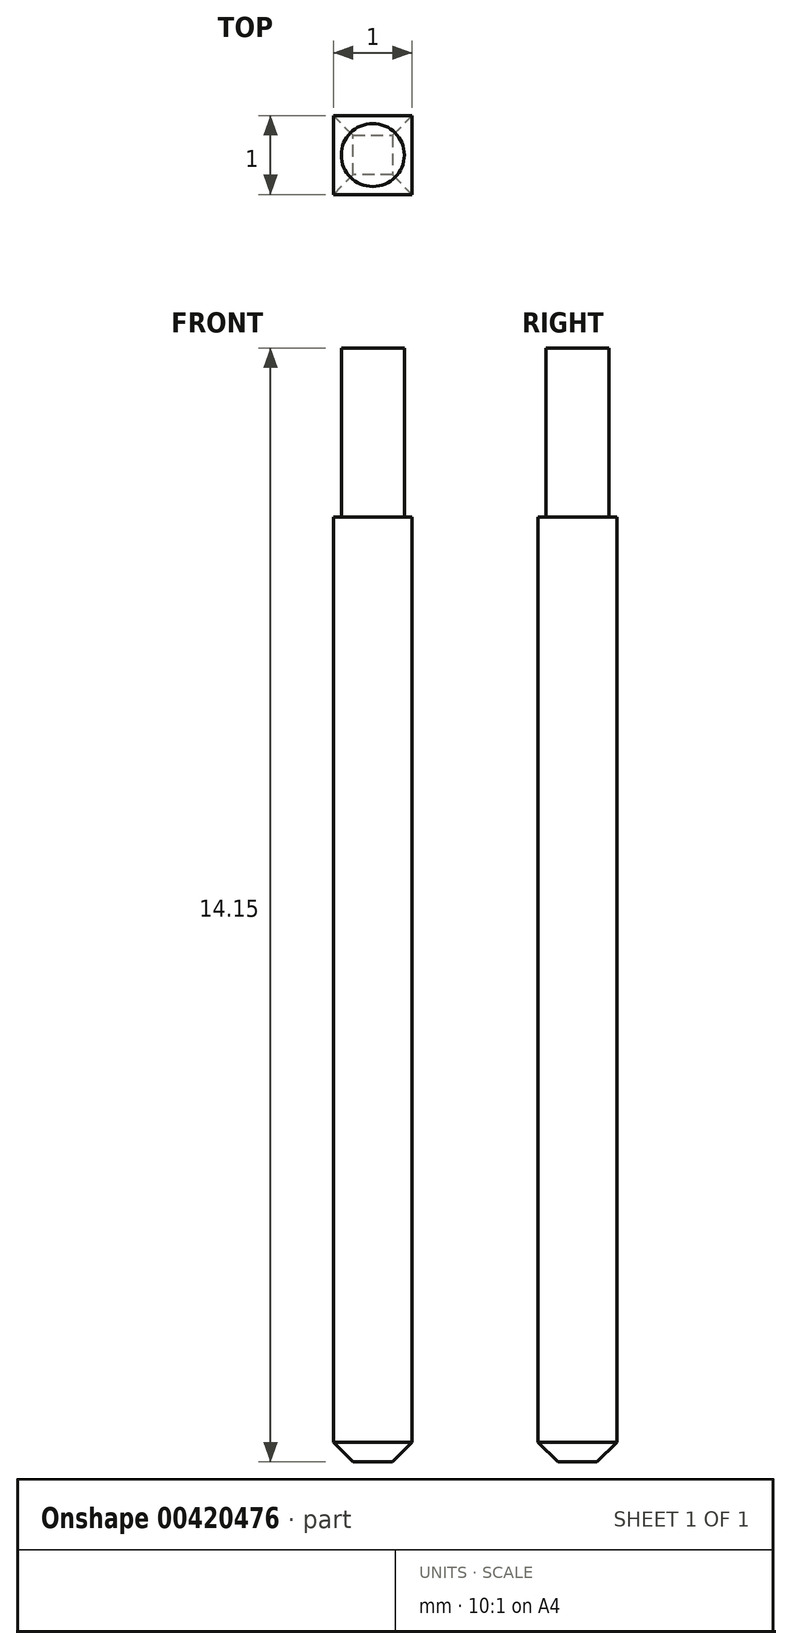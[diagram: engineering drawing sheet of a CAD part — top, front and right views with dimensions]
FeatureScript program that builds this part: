
annotation { "Feature Type Name" : "Feature", "Feature Type Description" : "" }
export const myFeature = defineFeature(function(context is Context, id is Id, definition is map)
    precondition{}
    {
        {
            var Q0;
            Q0=qCreatedBy(makeId("Top.planeOp"),FACE);
            var sketch = newSketch(context, id + "F0", { "sketchPlane" : qUnion([Q0])});
            skLineSegment(sketch, "E0.bottom", {"start": v(0, 0) * mm, "end": v(1, 0) * mm});
            skLineSegment(sketch, "E0.top", {"start": v(0, 1) * mm, "end": v(1, 1) * mm});
            skLineSegment(sketch, "E0.left", {"start": v(0, 0) * mm, "end": v(0, 1) * mm});
            skLineSegment(sketch, "E0.right", {"start": v(1, 0) * mm, "end": v(1, 1) * mm});
            skSolve(sketch);
        }
        {
            var Q0;
            Q0 = qSketchRegion(id + "F0", true);
            extrude(context, id + "F1", {"entities" : qUnion([Q0]), "depth" : 12 * mm});
        }
        {
            var Q0;
            Q0=makeQuery(id+"F1.opExtrude","CAP_FACE",FACE,{"disambiguationData":[OSD([sQuery(id+"F0.wireOp",EDGE,"E0.bottom"),sQuery(id+"F0.wireOp",EDGE,"E0.top"),sQuery(id+"F0.wireOp",EDGE,"E0.left"),sQuery(id+"F0.wireOp",EDGE,"E0.right")])],"isStart":false});
            var sketch = newSketch(context, id + "F2", { "sketchPlane" : qUnion([Q0])});
            skCircle(sketch, "E1", {"center": v(0.5, 0.5) * mm, "radius": 0.4 * mm});
            skPoint(sketch, "E1.centerSnap0", {"position": v(1, 0.5) * mm});
            skSolve(sketch);
        }
        {
            var Q0;
            Q0 = qSketchRegion(id + "F2", true);
            extrude(context, id + "F3", {"entities" : qUnion([Q0]), "operationType" : NewBodyOperationType.ADD, "depth" : 2.15 * mm});
        }
        {
            var Q0;
            Q0=makeQuery(id+"F1.opExtrude","CAP_EDGE",EDGE,{"disambiguationData":[OSD([sQuery(id+"F0.wireOp",EDGE,"E0.bottom")])],"isStart":true});
            var Q1;
            Q1=makeQuery(id+"F1.opExtrude","CAP_EDGE",EDGE,{"disambiguationData":[OSD([sQuery(id+"F0.wireOp",EDGE,"E0.left")])],"isStart":true});
            var Q2;
            Q2=makeQuery(id+"F1.opExtrude","CAP_EDGE",EDGE,{"disambiguationData":[OSD([sQuery(id+"F0.wireOp",EDGE,"E0.right")])],"isStart":true});
            var Q3;
            Q3=makeQuery(id+"F1.opExtrude","CAP_EDGE",EDGE,{"disambiguationData":[OSD([sQuery(id+"F0.wireOp",EDGE,"E0.top")])],"isStart":true});
            chamfer(context, id + "F4", {"entities" : qUnion([Q0, Q1, Q2, Q3]), "width" : 0.25 * mm, "tangentPropagation" : true});
        }
    });
